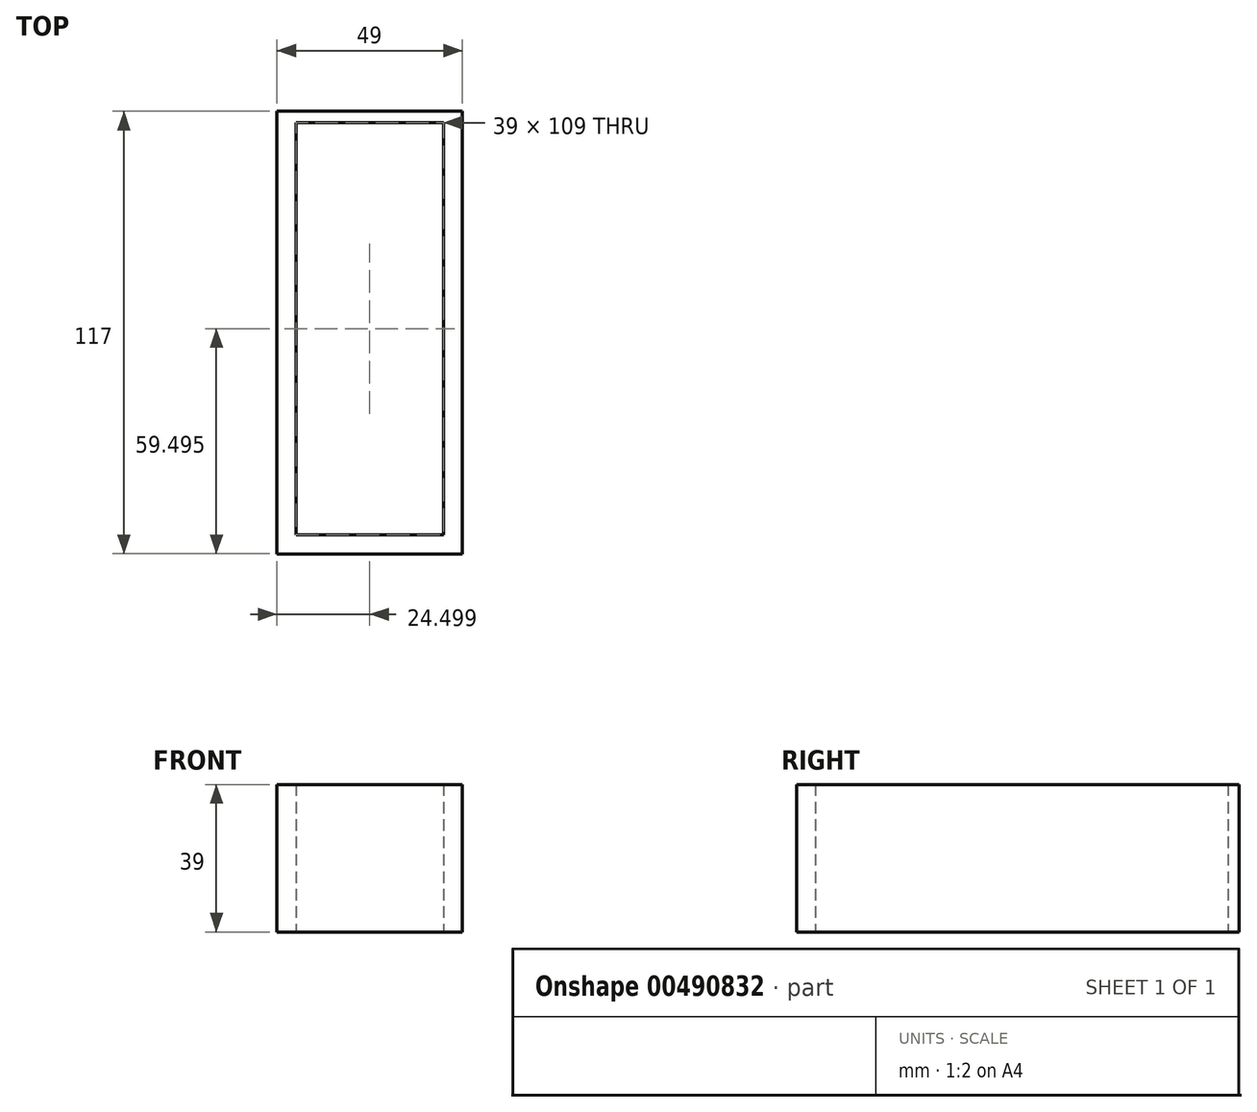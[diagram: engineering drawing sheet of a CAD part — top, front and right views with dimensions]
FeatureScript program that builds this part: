
annotation { "Feature Type Name" : "Feature", "Feature Type Description" : "" }
export const myFeature = defineFeature(function(context is Context, id is Id, definition is map)
    precondition{}
    {
        {
            var Q0;
            Q0=qCreatedBy(makeId("Top.planeOp"),FACE);
            var sketch = newSketch(context, id + "F0", { "sketchPlane" : qUnion([Q0])});
            skLineSegment(sketch, "E0", {"start": v(25.67, 87.97) * mm, "end": v(-18.33, 87.97) * mm});
            skLineSegment(sketch, "E1", {"start": v(-18.33, 87.97) * mm, "end": v(-18.33, -29.03) * mm});
            skLineSegment(sketch, "E2", {"start": v(-18.33, -29.03) * mm, "end": v(25.67, -29.03) * mm});
            skLineSegment(sketch, "E3", {"start": v(25.67, -24.03) * mm, "end": v(-13.33, -24.03) * mm});
            skLineSegment(sketch, "E4", {"start": v(-13.33, -24.03) * mm, "end": v(-13.33, 84.97) * mm});
            skLineSegment(sketch, "E5", {"start": v(-13.33, 84.97) * mm, "end": v(25.67, 84.97) * mm});
            skLineSegment(sketch, "E6", {"start": v(25.67, 87.97) * mm, "end": v(30.67, 87.97) * mm});
            skLineSegment(sketch, "E7", {"start": v(30.67, 87.97) * mm, "end": v(30.67, -29.03) * mm});
            skLineSegment(sketch, "E8", {"start": v(30.67, -29.03) * mm, "end": v(25.67, -29.03) * mm});
            skLineSegment(sketch, "E9", {"start": v(25.67, -24.03) * mm, "end": v(25.67, 84.97) * mm});
            skSolve(sketch);
        }
        {
            var Q0;
            Q0=makeQuery(id+"F0.imprint","IMPRINT",FACE,{"disambiguationData":[TD([[makeQuery(id+"F0.imprint","IMPRINT",EDGE,{"derivedFrom":sQuery(id+"F0.wireOp",EDGE,"E0")}),1.0]])]});
            extrude(context, id + "F1", {"entities" : qUnion([Q0]), "depth" : 39 * mm, "offsetDistance" : 25 * mm});
        }
    });
